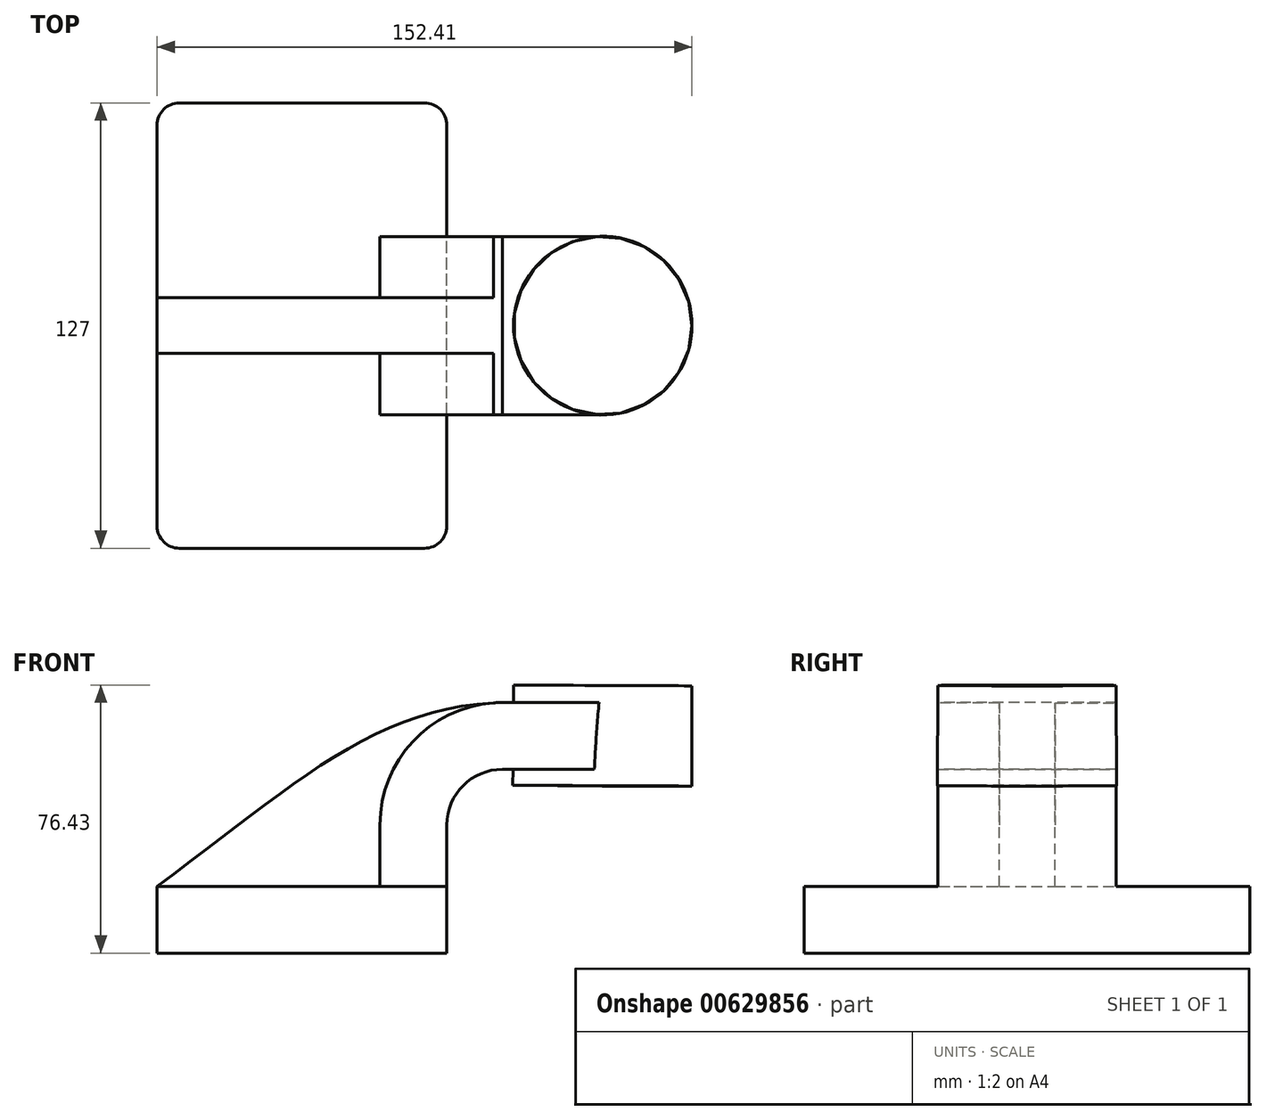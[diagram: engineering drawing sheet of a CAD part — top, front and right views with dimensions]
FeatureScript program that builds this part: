
annotation { "Feature Type Name" : "Feature", "Feature Type Description" : "" }
export const myFeature = defineFeature(function(context is Context, id is Id, definition is map)
    precondition{}
    {
        {
            var Q0;
            Q0=qCreatedBy(makeId("Front.planeOp"),FACE);
            var sketch = newSketch(context, id + "F0", { "sketchPlane" : qUnion([Q0])});
            skLineSegment(sketch, "E0.bottom", {"start": v(-41.27, -8.75) * mm, "end": v(41.27, -8.75) * mm});
            skLineSegment(sketch, "E0.top", {"start": v(-41.28, 10.3) * mm, "end": v(41.27, 10.3) * mm});
            skLineSegment(sketch, "E0.left", {"start": v(-41.28, -8.75) * mm, "end": v(-41.28, 10.3) * mm});
            skLineSegment(sketch, "E0.right", {"start": v(41.28, -8.75) * mm, "end": v(41.28, 10.3) * mm});
            skPoint(sketch, "E0.middle", {"position": v(0, 0.78) * mm});
            skLineSegment(sketch, "E1.bottom", {"start": v(60.33, 38.88) * mm, "end": v(111.13, 38.88) * mm});
            skLineSegment(sketch, "E1.top", {"start": v(60.33, 67.45) * mm, "end": v(111.13, 67.45) * mm});
            skLineSegment(sketch, "E1.left", {"start": v(60.33, 38.88) * mm, "end": v(60.33, 67.45) * mm});
            skLineSegment(sketch, "E1.right", {"start": v(111.13, 38.88) * mm, "end": v(111.13, 67.45) * mm});
            skPoint(sketch, "E1.middle", {"position": v(85.73, 53.17) * mm});
            skLineSegment(sketch, "E2", {"start": v(41.28, 10.3) * mm, "end": v(41.28, 27.78) * mm});
            skArc(sketch, "E3", {"start": v(41.28, 27.78) * mm, "mid": v(45.92, 39) * mm, "end": v(57.15, 43.65) * mm});
            skLineSegment(sketch, "E4", {"start": v(57.15, 43.65) * mm, "end": v(85.6, 43.65) * mm});
            skLineSegment(sketch, "E5.0", {"start": v(57.15, 62.7) * mm, "end": v(85.6, 62.7) * mm});
            skArc(sketch, "E5.1", {"start": v(22.23, 27.78) * mm, "mid": v(32.45, 52.47) * mm, "end": v(57.15, 62.7) * mm});
            skLineSegment(sketch, "E5.2", {"start": v(22.23, 10.3) * mm, "end": v(22.23, 27.78) * mm});
            skLineSegment(sketch, "E6", {"start": v(85.73, 67.45) * mm, "end": v(85.6, 38.88) * mm});
            skFitSpline(sketch, "E7", {"points": [v(-41.28, 10.3) * mm, v(57.15, 62.7) * mm], "startDerivative": vector(114.15, 84.1) * mm, "endDerivative": vector(110.52, 2.49) * mm});
            skLineSegment(sketch, "E8", {"start": v(85.6, 43.65) * mm, "end": v(85.6, 62.7) * mm});
            skSolve(sketch);
        }
        {
            var Q0;
            Q0=makeQuery(id+"F0.imprint","IMPRINT",FACE,{"disambiguationData":[TD([[makeQuery(id+"F0.imprint","IMPRINT",EDGE,{"derivedFrom":sQuery(id+"F0.wireOp",EDGE,"E0.bottom")}),1.0]])]});
            extrude(context, id + "F1", {"entities" : qUnion([Q0]), "endBound" : BoundingType.SYMMETRIC, "depth" : 127 * mm, "offsetDistance" : 25.4 * mm});
        }
        {
            var Q0;
            {var subQ5=sQuery(id+"F0.wireOp",EDGE,"E8");Q0=makeQuery(id+"F0.imprint","IMPRINT",FACE,{"disambiguationData":[TD([[makeQuery(id+"F0.imprint","IMPRINT",EDGE,{"derivedFrom":subQ5}),1.0]])]});}
            var Q1;
            {var subQ1=sQuery(id+"F0.wireOp",EDGE,"E2");Q1=makeQuery(id+"F0.imprint","IMPRINT",FACE,{"disambiguationData":[TD([[makeQuery(id+"F0.imprint","IMPRINT",EDGE,{"derivedFrom":subQ1}),1.0]])]});}
            extrude(context, id + "F2", {"entities" : qUnion([Q0, Q1]), "operationType" : NewBodyOperationType.ADD, "endBound" : BoundingType.SYMMETRIC, "depth" : 50.8 * mm, "offsetDistance" : 25.4 * mm});
        }
        {
            var Q0;
            {var subQ3=sQuery(id+"F0.wireOp",EDGE,"E5.2");Q0=makeQuery(id+"F0.imprint","IMPRINT",FACE,{"disambiguationData":[TD([[makeQuery(id+"F0.imprint","IMPRINT",EDGE,{"derivedFrom":subQ3}),1.0]])]});}
            extrude(context, id + "F3", {"entities" : qUnion([Q0]), "operationType" : NewBodyOperationType.ADD, "endBound" : BoundingType.SYMMETRIC, "depth" : 15.88 * mm, "offsetDistance" : 25.4 * mm});
        }
        {
            var Q0;
            {var subQ0=sQuery(id+"F0.wireOp",EDGE,"E1.right");Q0=makeQuery(id+"F0.imprint","IMPRINT",FACE,{"disambiguationData":[TD([[makeQuery(id+"F0.imprint","IMPRINT",EDGE,{"derivedFrom":subQ0}),1.0]])]});}
            var Q1;
            Q1=sQuery(id+"F0.wireOp",EDGE,"E6");
            revolve(context, id + "F4", {"operationType" : NewBodyOperationType.ADD, "entities" : qUnion([Q0]), "axis" : qUnion([Q1]), "revolveType" : RevolveType.FULL});
        }
        {
            var Q0;
            Q0=makeQuery(id+"F1.opExtrude","CAP_EDGE",EDGE,{"disambiguationData":[OSD([sQuery(id+"F0.wireOp",EDGE,"E0.right")])],"isStart":true});
            var Q1;
            Q1=makeQuery(id+"F1.opExtrude","CAP_EDGE",EDGE,{"disambiguationData":[OSD([sQuery(id+"F0.wireOp",EDGE,"E0.left")])],"isStart":true});
            var Q2;
            Q2=makeQuery(id+"F1.opExtrude","CAP_EDGE",EDGE,{"disambiguationData":[OSD([sQuery(id+"F0.wireOp",EDGE,"E0.right")])],"isStart":false});
            var Q3;
            Q3=makeQuery(id+"F1.opExtrude","CAP_EDGE",EDGE,{"disambiguationData":[OSD([sQuery(id+"F0.wireOp",EDGE,"E0.left")])],"isStart":false});
            fillet(context, id + "F5", {"entities" : qUnion([Q0, Q1, Q2, Q3]), "radius" : 6.35 * mm, "tangentPropagation" : true, "allowEdgeOverflow" : false});
        }
    });
